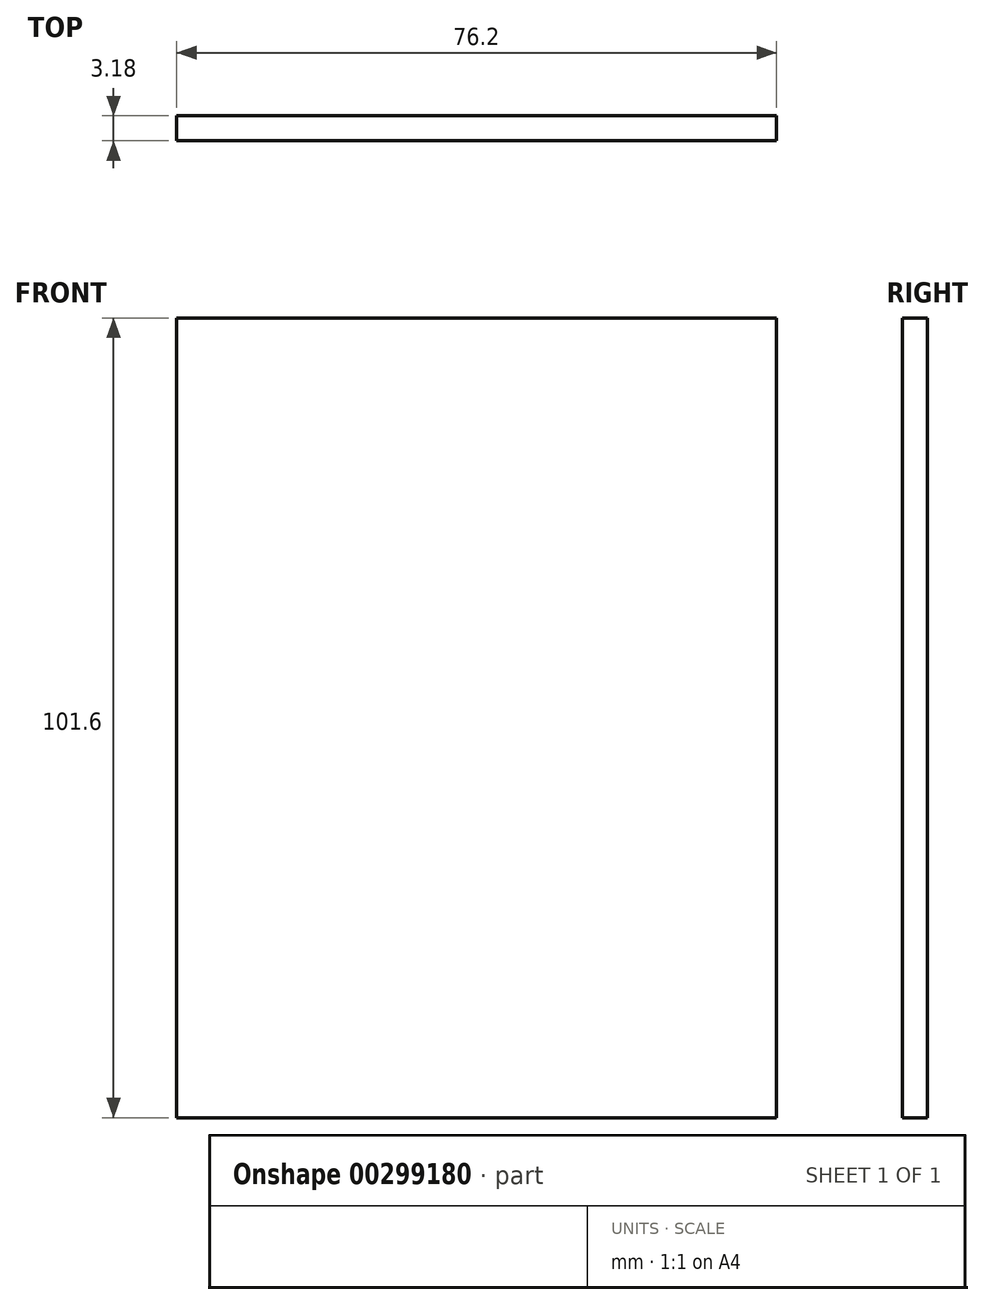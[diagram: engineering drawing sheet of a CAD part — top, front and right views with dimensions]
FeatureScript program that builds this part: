
annotation { "Feature Type Name" : "Feature", "Feature Type Description" : "" }
export const myFeature = defineFeature(function(context is Context, id is Id, definition is map)
    precondition{}
    {
        {
            var Q0;
            Q0=qCreatedBy(makeId("Front.planeOp"),FACE);
            var sketch = newSketch(context, id + "F0", { "sketchPlane" : qUnion([Q0])});
            skLineSegment(sketch, "E0.bottom", {"start": v(38.1, 50.8) * mm, "end": v(-38.1, 50.8) * mm});
            skLineSegment(sketch, "E0.top", {"start": v(38.1, -50.8) * mm, "end": v(-38.1, -50.8) * mm});
            skLineSegment(sketch, "E0.left", {"start": v(38.1, 50.8) * mm, "end": v(38.1, -50.8) * mm});
            skLineSegment(sketch, "E0.right", {"start": v(-38.1, 50.8) * mm, "end": v(-38.1, -50.8) * mm});
            skPoint(sketch, "E0.middle", {"position": v(0, 0) * mm});
            skSolve(sketch);
        }
        {
            var Q0;
            Q0 = qSketchRegion(id + "F0", true);
            extrude(context, id + "F1", {"entities" : qUnion([Q0]), "endBound" : BoundingType.SYMMETRIC, "depth" : 3.17 * mm});
        }
    });
